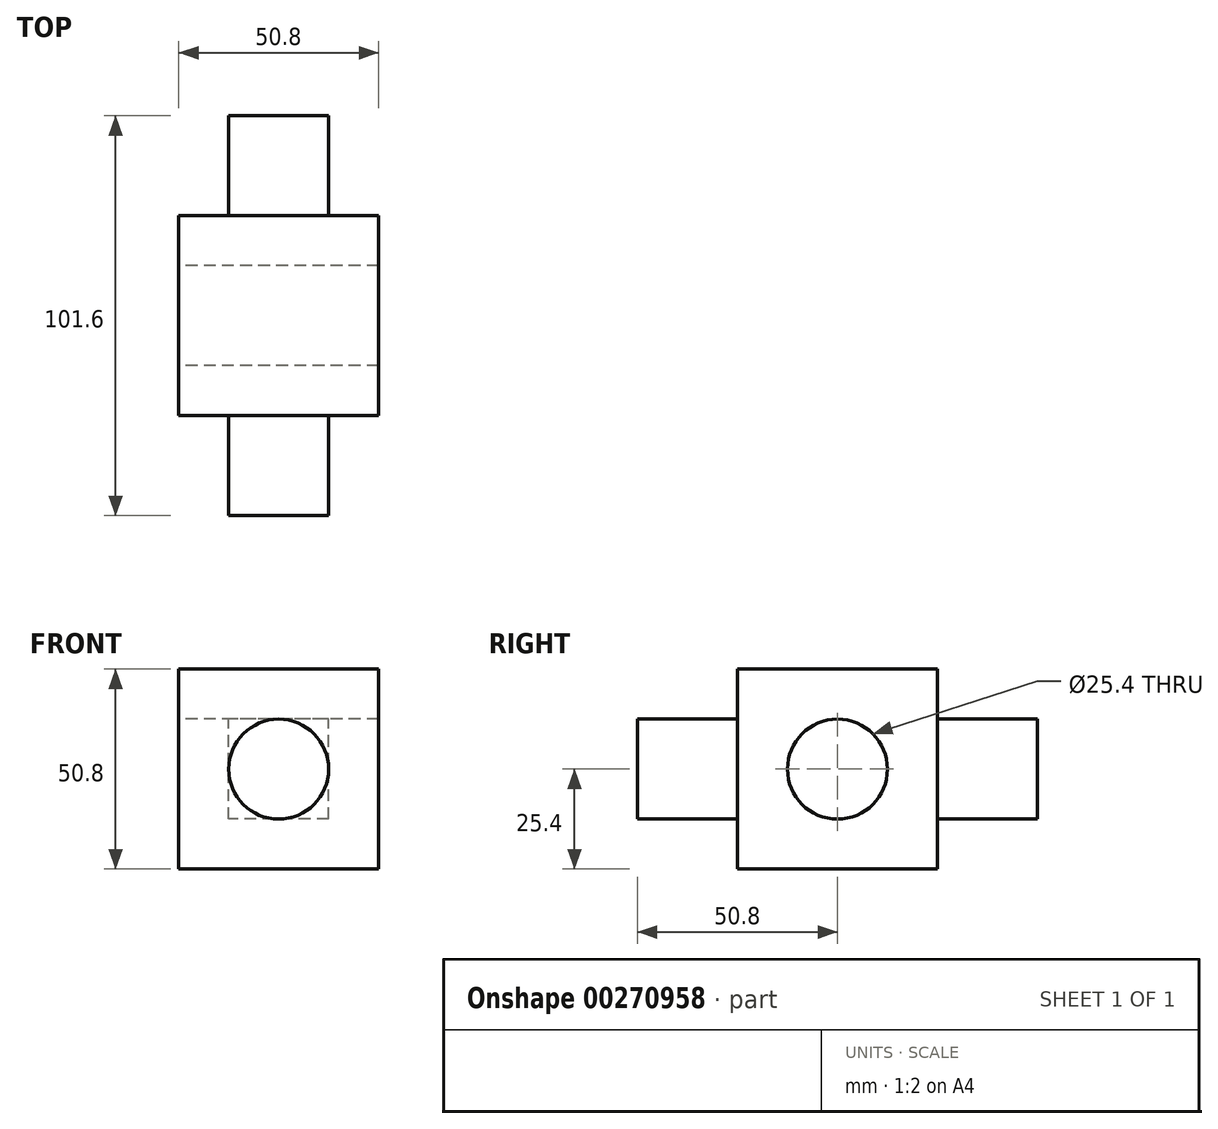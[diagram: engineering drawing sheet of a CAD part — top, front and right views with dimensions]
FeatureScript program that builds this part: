
annotation { "Feature Type Name" : "Feature", "Feature Type Description" : "" }
export const myFeature = defineFeature(function(context is Context, id is Id, definition is map)
    precondition{}
    {
        {
            var Q0;
            Q0=qCreatedBy(makeId("Front.planeOp"),FACE);
            var sketch = newSketch(context, id + "F0", { "sketchPlane" : qUnion([Q0])});
            skLineSegment(sketch, "E0.bottom", {"start": v(0, 0) * mm, "end": v(-50.8, 0) * mm});
            skLineSegment(sketch, "E0.top", {"start": v(0, 50.8) * mm, "end": v(-50.8, 50.8) * mm});
            skLineSegment(sketch, "E0.left", {"start": v(0, 0) * mm, "end": v(0, 50.8) * mm});
            skLineSegment(sketch, "E0.right", {"start": v(-50.8, 0) * mm, "end": v(-50.8, 50.8) * mm});
            skSolve(sketch);
        }
        {
            var Q0;
            Q0 = qSketchRegion(id + "F0", true);
            extrude(context, id + "F1", {"entities" : qUnion([Q0]), "depth" : 50.8 * mm});
        }
        {
            var Q0;
            Q0=makeQuery(id+"F1.opExtrude","CAP_FACE",FACE,{"disambiguationData":[OSD([sQuery(id+"F0.wireOp",EDGE,"E0.bottom"),sQuery(id+"F0.wireOp",EDGE,"E0.top"),sQuery(id+"F0.wireOp",EDGE,"E0.left"),sQuery(id+"F0.wireOp",EDGE,"E0.right")])],"isStart":false});
            var sketch = newSketch(context, id + "F2", { "sketchPlane" : qUnion([Q0])});
            skCircle(sketch, "E1", {"center": v(-25.4, 25.4) * mm, "radius": 12.7 * mm});
            skSolve(sketch);
        }
        {
            var Q0;
            Q0 = qSketchRegion(id + "F2", true);
            extrude(context, id + "F3", {"entities" : qUnion([Q0]), "operationType" : NewBodyOperationType.ADD, "depth" : 25.4 * mm});
        }
        {
            var Q0;
            Q0=makeQuery(id+"F1.opExtrude","SWEPT_FACE",FACE,{"disambiguationData":[OSD([sQuery(id+"F0.wireOp",EDGE,"E0.right")])]});
            var sketch = newSketch(context, id + "F4", { "sketchPlane" : qUnion([Q0])});
            skCircle(sketch, "E2", {"center": v(25.4, 25.4) * mm, "radius": 12.7 * mm});
            skSolve(sketch);
        }
        {
            var Q0;
            Q0 = qSketchRegion(id + "F4", true);
            extrude(context, id + "F5", {"entities" : qUnion([Q0]), "operationType" : NewBodyOperationType.REMOVE, "oppositeDirection" : true, "depth" : 50.8 * mm});
        }
        {
            var Q0;
            Q0=makeQuery(id+"F1.opExtrude","CAP_FACE",FACE,{"disambiguationData":[OSD([sQuery(id+"F0.wireOp",EDGE,"E0.bottom"),sQuery(id+"F0.wireOp",EDGE,"E0.top"),sQuery(id+"F0.wireOp",EDGE,"E0.left"),sQuery(id+"F0.wireOp",EDGE,"E0.right")])],"isStart":true});
            var sketch = newSketch(context, id + "F6", { "sketchPlane" : qUnion([Q0])});
            skLineSegment(sketch, "E3.bottom", {"start": v(12.7, 12.7) * mm, "end": v(38.1, 12.7) * mm});
            skLineSegment(sketch, "E3.top", {"start": v(12.7, 38.1) * mm, "end": v(38.1, 38.1) * mm});
            skLineSegment(sketch, "E3.left", {"start": v(12.7, 12.7) * mm, "end": v(12.7, 38.1) * mm});
            skLineSegment(sketch, "E3.right", {"start": v(38.1, 12.7) * mm, "end": v(38.1, 38.1) * mm});
            skSolve(sketch);
        }
        {
            var Q0;
            Q0 = qSketchRegion(id + "F6", true);
            extrude(context, id + "F7", {"entities" : qUnion([Q0]), "operationType" : NewBodyOperationType.ADD, "depth" : 25.4 * mm});
        }
    });
